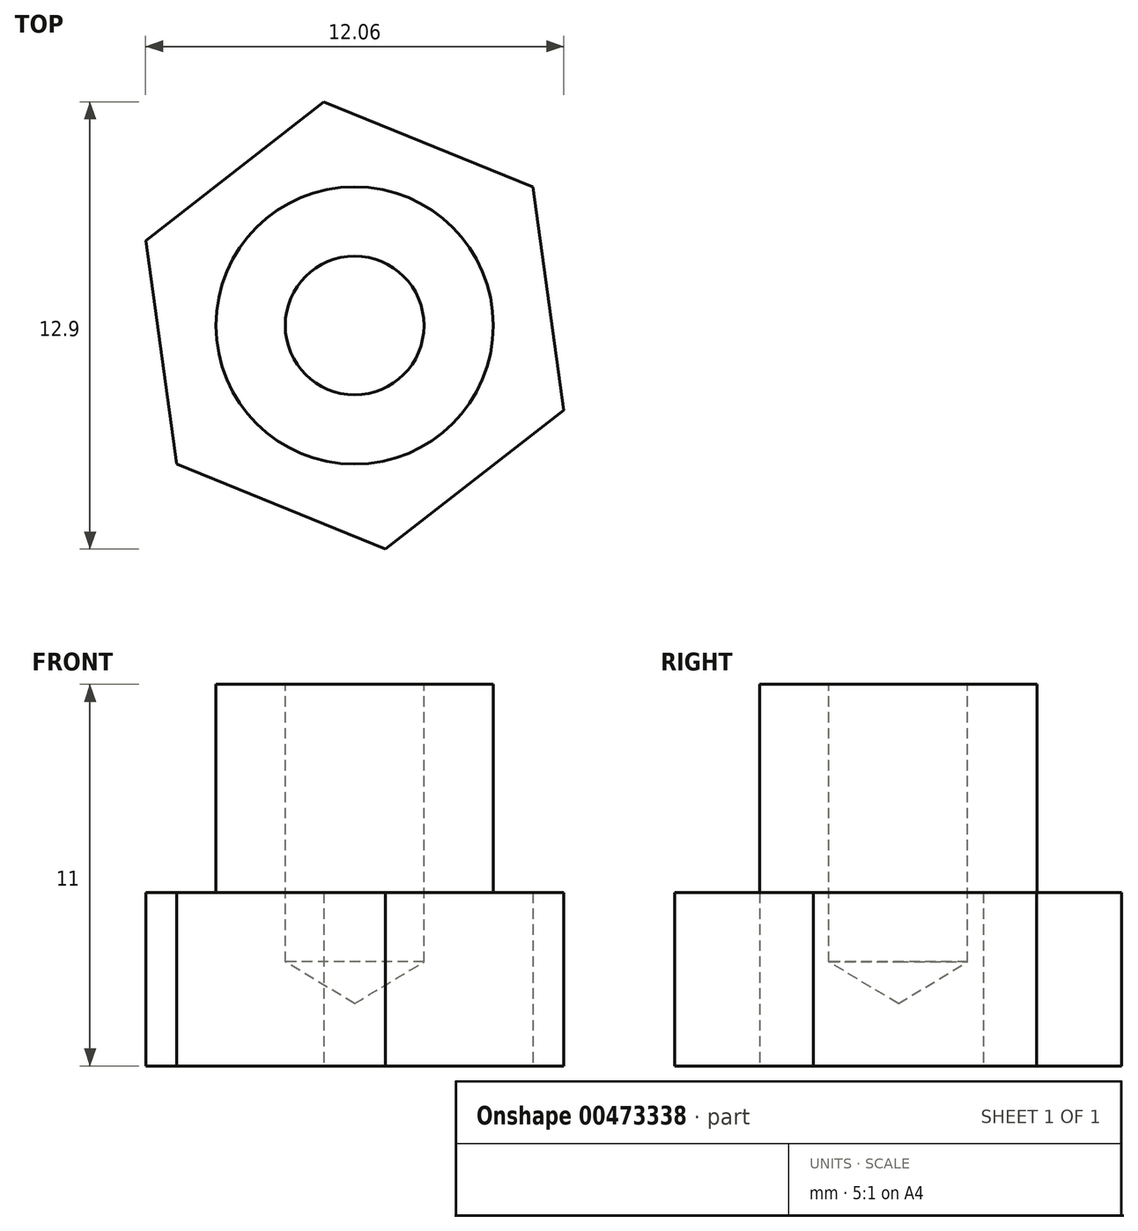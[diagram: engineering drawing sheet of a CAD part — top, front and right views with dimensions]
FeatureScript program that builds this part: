
annotation { "Feature Type Name" : "Feature", "Feature Type Description" : "" }
export const myFeature = defineFeature(function(context is Context, id is Id, definition is map)
    precondition{}
    {
        {
            var Q0;
            Q0=qCreatedBy(makeId("Top.planeOp"),FACE);
            var sketch = newSketch(context, id + "F0", { "sketchPlane" : qUnion([Q0])});
            skCircle(sketch, "E0", {"center": v(0, 0) * mm, "radius": 4 * mm});
            skSolve(sketch);
        }
        {
            var Q0;
            Q0 = qSketchRegion(id + "F0", true);
            extrude(context, id + "F1", {"entities" : qUnion([Q0]), "depth" : 11 * mm});
        }
        {
            var Q0;
            Q0=qCreatedBy(makeId("Top.planeOp"),FACE);
            var sketch = newSketch(context, id + "F2", { "sketchPlane" : qUnion([Q0])});
            skCircle(sketch, "E1.cCircle", {"center": v(0, 0) * mm, "radius": 5.64 * mm, "construction": true});
            skLineSegment(sketch, "E1.0", {"start": v(6.03, -2.45) * mm, "end": v(0.9, -6.45) * mm});
            skLineSegment(sketch, "E1.1", {"start": v(0.9, -6.45) * mm, "end": v(-5.14, -4) * mm});
            skLineSegment(sketch, "E1.2", {"start": v(-5.14, -4) * mm, "end": v(-6.03, 2.45) * mm});
            skLineSegment(sketch, "E1.3", {"start": v(-6.03, 2.45) * mm, "end": v(-0.9, 6.45) * mm});
            skLineSegment(sketch, "E1.4", {"start": v(-0.9, 6.45) * mm, "end": v(5.14, 4) * mm});
            skLineSegment(sketch, "E1.5", {"start": v(5.14, 4) * mm, "end": v(6.03, -2.45) * mm});
            skPoint(sketch, "E1.0.midPoint", {"position": v(3.46, -4.45) * mm});
            skSolve(sketch);
        }
        {
            var Q0;
            Q0=makeQuery(id+"F2.imprint","IMPRINT",FACE,{"disambiguationData":[TD([[makeQuery(id+"F2.imprint","IMPRINT",EDGE,{"derivedFrom":sQuery(id+"F2.wireOp",EDGE,"E1.0")}),-1.0]])]});
            extrude(context, id + "F3", {"entities" : qUnion([Q0]), "operationType" : NewBodyOperationType.ADD, "depth" : 5 * mm});
        }
        {
            var Q0;
            Q0=qCreatedBy(makeId("Top.planeOp"),FACE);
            cPlane(context, id + "F4", {"entities" : qUnion([Q0]), "cplaneType" : CPlaneType.OFFSET, "offset" : 11 * mm, "width" : 150 * mm, "height" : 150 * mm});
        }
        {
            var Q0;
            Q0=qCreatedBy(id+"F4.planeOp",FACE);
            var sketch = newSketch(context, id + "F5", { "sketchPlane" : qUnion([Q0])});
            skPoint(sketch, "E2", {"position": v(0, 0) * mm});
            skSolve(sketch);
        }
        {
            var Q0;
            Q0=sQuery(id+"F5.wireOp",VERTEX,"E2");
            var Q1;
            Q1=makeQuery(id+"F1.opExtrude","SWEPT_BODY",BODY,{"disambiguationData":[OSD([sQuery(id+"F0.wireOp",EDGE,"E0")])]});
            hole(context, id + "F6", {"style" : HoleStyle.SIMPLE, "endStyle" : HoleEndStyle.BLIND, "holeDiameter" : 4 * mm, "holeDepth" : 8 * mm, "isTappedThrough" : true, "tappedDepth" : 12 * mm, "tapClearance" : 3, "startFromSketch" : true, "locations" : qUnion([Q0]), "scope" : qUnion([Q1])});
        }
    });
